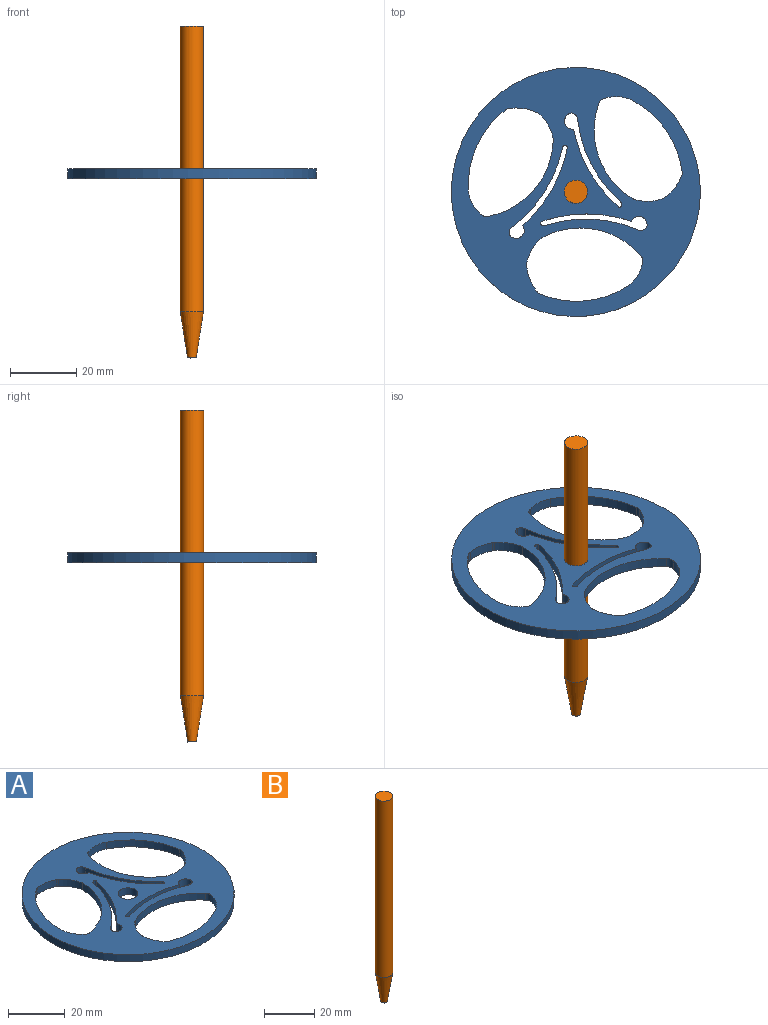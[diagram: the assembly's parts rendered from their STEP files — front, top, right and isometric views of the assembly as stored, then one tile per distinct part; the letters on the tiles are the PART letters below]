
ASSEMBLY  parts=2 mates=1
PART A: 54 faces, bbox 75x75x3 mm
  f0: cylinder r=2.29mm len=3mm, axis (0,0,-1), area 8.3mm2, adj f1,f45,f52,f53
  f1: cylinder r=39.9mm len=23.61mm, axis (0,0,-1), area 85.9mm2, adj f0,f2,f52,f53
  f2: cylinder r=0.98mm len=3mm, axis (0,0,-1), area 4.4mm2, adj f1,f3,f52,f53
  f3: cylinder r=0.6mm len=3mm, axis (0,0,-1), area 3.2mm2, adj f2,f4,f52,f53
  f4: cylinder r=42.15mm len=23.38mm, axis (0,0,-1), area 82.5mm2, adj f3,f45,f52,f53
  f5: cylinder r=2.29mm len=3mm, axis (0,0,-1), area 8.3mm2, adj f6,f46,f52,f53
  f6: cylinder r=39.9mm len=24.88mm, axis (0,0,-1), area 85.9mm2, adj f5,f7,f52,f53
  f7: cylinder r=0.98mm len=3mm, axis (0,0,-1), area 4.4mm2, adj f6,f8,f52,f53
  f8: cylinder r=0.6mm len=3mm, axis (0,0,-1), area 3.2mm2, adj f7,f9,f52,f53
  f9: cylinder r=42.15mm len=23.38mm, axis (0,0,-1), area 82.5mm2, adj f8,f46,f52,f53
  f10: cylinder r=2.29mm len=3mm, axis (0,0,-1), area 8.3mm2, adj f11,f47,f52,f53
  f11: cylinder r=39.9mm len=28mm, axis (0,0,-1), area 85.9mm2, adj f10,f12,f52,f53
  f12: cylinder r=0.98mm len=3mm, axis (0,0,-1), area 4.4mm2, adj f11,f13,f52,f53
  f13: cylinder r=0.6mm len=3mm, axis (0,0,-1), area 3.2mm2, adj f12,f14,f52,f53
  f14: cylinder r=42.15mm len=27mm, axis (0,0,-1), area 82.5mm2, adj f13,f47,f52,f53
  f15: cylinder r=2.2mm len=3mm, axis (0,0,-1), area 7.3mm2, adj f16,f48,f52,f53
  f16: cylinder r=10.61mm len=6.93mm, axis (0,0,-1), area 25.3mm2, adj f15,f17,f52,f53
  f17: cylinder r=28.47mm len=26.36mm, axis (0,0,-1), area 82.6mm2, adj f16,f18,f52,f53
  f18: cylinder r=2.41mm len=3mm, axis (0,0,-1), area 4.4mm2, adj f17,f19,f52,f53
  f19: cylinder r=14.07mm len=7.7mm, axis (0,0,-1), area 25.2mm2, adj f18,f20,f52,f53
  f20: cylinder r=2.28mm len=3mm, axis (0,0,-1), area 2mm2, adj f19,f21,f52,f53
  f21: cylinder r=12.91mm len=7.56mm, axis (0,0,-1), area 26.6mm2, adj f20,f22,f52,f53
  f22: cylinder r=0.82mm len=3mm, axis (0,0,-1), area 0.2mm2, adj f21,f23,f52,f53
  f23: cylinder r=12.91mm len=3mm, axis (0,0,-1), area 0.1mm2, adj f22,f24,f52,f53
  f24: plane 3x0.01mm, normal (0.49,-0.87,0), area 0mm2, adj f23,f25,f52,f53
  f25: cylinder r=0.82mm len=3mm, axis (0,0,-1), area 0.5mm2, adj f24,f48,f52,f53
  f26: cylinder r=2.41mm len=3mm, axis (0,0,-1), area 4.4mm2, adj f27,f49,f52,f53
  f27: cylinder r=14.07mm len=6.46mm, axis (0,0,-1), area 25.2mm2, adj f26,f28,f52,f53
  f28: cylinder r=2.28mm len=3mm, axis (0,0,-1), area 2mm2, adj f27,f29,f52,f53
  f29: cylinder r=12.91mm len=8.7mm, axis (0,0,-1), area 26.6mm2, adj f28,f30,f52,f53
  f30: cylinder r=0.82mm len=3mm, axis (0,0,-1), area 0.2mm2, adj f29,f31,f52,f53
  f31: cylinder r=12.91mm len=3mm, axis (0,0,-1), area 0.1mm2, adj f30,f32,f52,f53
  f32: plane 3x0.01mm, normal (0.51,0.86,0), area 0mm2, adj f31,f33,f52,f53
  f33: cylinder r=24.06mm len=28.56mm, axis (0,0,-1), area 98.7mm2, adj f32,f34,f52,f53
  f34: cylinder r=2.2mm len=3mm, axis (0,0,-1), area 7.3mm2, adj f33,f35,f52,f53
  f35: cylinder r=10.61mm len=8.2mm, axis (0,0,-1), area 25.3mm2, adj f34,f49,f52,f53
  f36: cylinder r=2.41mm len=3mm, axis (0,0,-1), area 4.4mm2, adj f37,f50,f52,f53
  f37: cylinder r=14.07mm len=8.17mm, axis (0,0,-1), area 25.2mm2, adj f36,f38,f52,f53
  f38: cylinder r=2.28mm len=3mm, axis (0,0,-1), area 2mm2, adj f37,f39,f52,f53
  f39: cylinder r=12.91mm len=7.51mm, axis (0,0,-1), area 26.6mm2, adj f38,f40,f52,f53
  f40: cylinder r=0.82mm len=3mm, axis (0,0,-1), area 0.4mm2, adj f39,f41,f52,f53
  f41: cylinder r=24.06mm len=23.28mm, axis (0,0,-1), area 98.7mm2, adj f40,f42,f52,f53
  f42: cylinder r=2.2mm len=3mm, axis (0,0,-1), area 7.3mm2, adj f41,f43,f52,f53
  f43: cylinder r=10.61mm len=7.28mm, axis (0,0,-1), area 25.3mm2, adj f42,f50,f52,f53
  f44: cylinder r=3.5mm len=7mm, axis (0,0,-1), area 66mm2, adj f52,f53
  f45: cylinder r=2.47mm len=4.46mm, axis (0,0,-1), area 23.2mm2, adj f0,f4,f52,f53
  f46: cylinder r=2.47mm len=4.92mm, axis (0,0,-1), area 23.2mm2, adj f5,f9,f52,f53
  f47: cylinder r=2.47mm len=4.72mm, axis (0,0,-1), area 23.2mm2, adj f10,f14,f52,f53
  f48: cylinder r=24.06mm len=29.78mm, axis (0,0,-1), area 98.2mm2, adj f15,f25,f52,f53
  f49: cylinder r=28.47mm len=21.61mm, axis (0,0,-1), area 82.6mm2, adj f26,f35,f52,f53
  f50: cylinder r=28.47mm len=24.05mm, axis (0,0,-1), area 82.6mm2, adj f36,f43,f52,f53
  f51: cylinder r=37.5mm len=75mm, axis (0,0,-1), area 706.9mm2, adj f52,f53
  f52: plane 75x75mm, normal (0,0,1), area 2399.8mm2, adj f0,f1,f2,f3,f4,f5,f6,f7
  f53: plane 75x75mm, normal (0,0,-1), area 2399.8mm2, adj f0,f1,f2,f3,f4,f5,f6,f7
PART B: 4 faces, bbox 7x7x100 mm
  f0: cylinder r=3.5mm len=86mm, axis (0,0,-1), area 1891.2mm2, adj f1,f3
  f1: plane 7x7mm, normal (0,0,1), area 38.5mm2, adj f0
  f2: plane 2.57x2.57mm, normal (0,0,-1), area 5.2mm2, adj f3
  f3: cone r=3.5mm half-angle=9deg, axis (0,0,1), area 213mm2, adj f0,f2
PLACE A t=(-86.4,-17.41,-67.15)mm
PLACE B t=(57.22,32.86,-121.15)mm
MATE fastened B.f0 <-> A.f51  axis (0,0,-1) through (-86.4,-17.41,-64.15)mm
